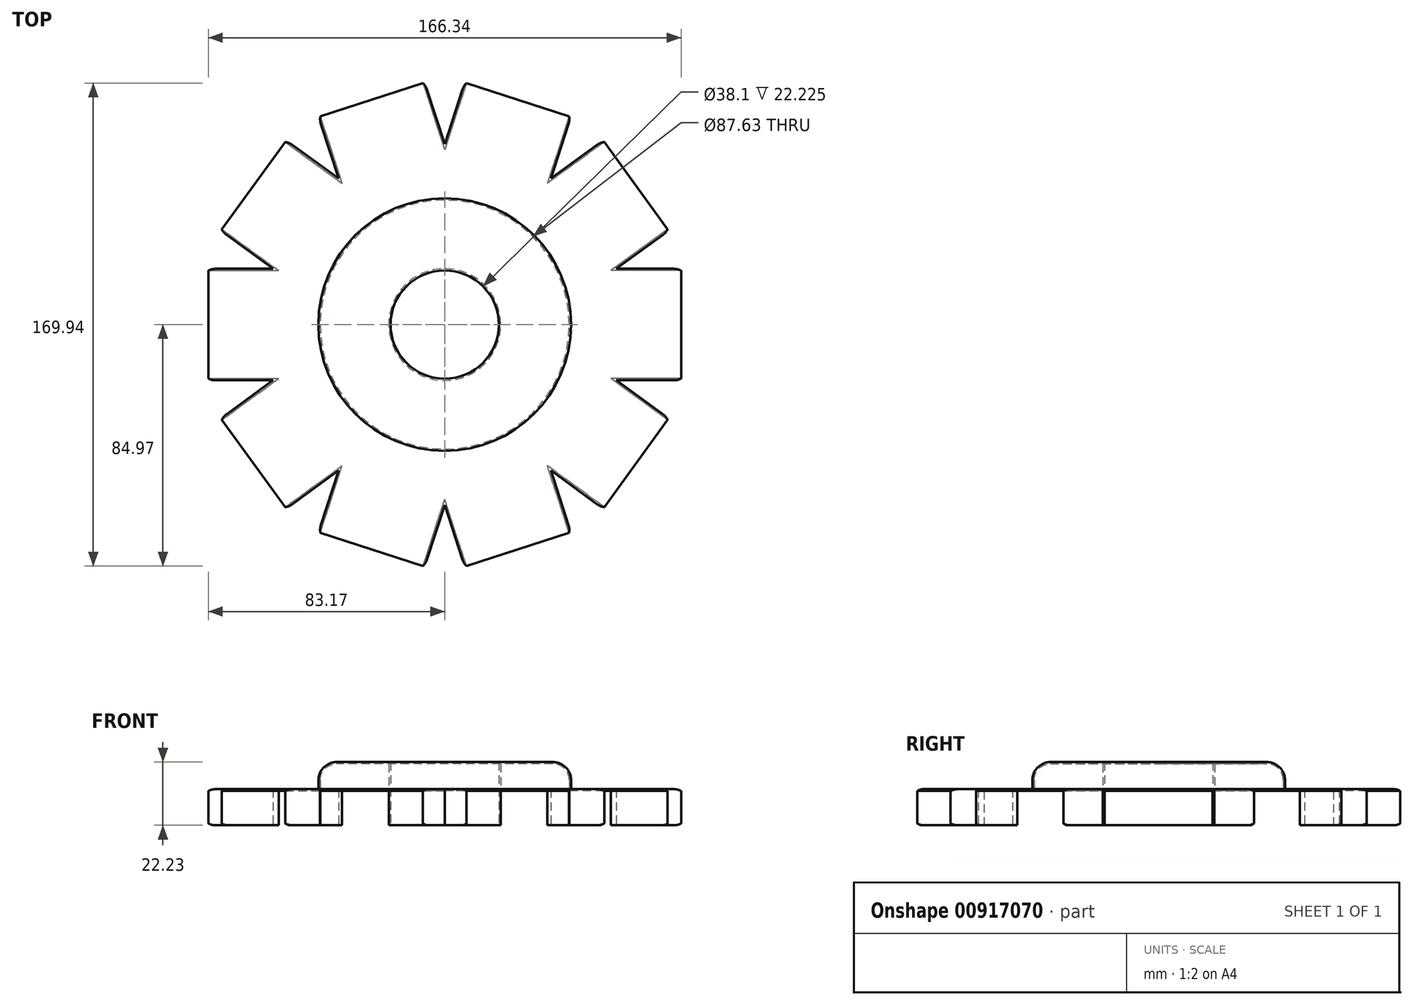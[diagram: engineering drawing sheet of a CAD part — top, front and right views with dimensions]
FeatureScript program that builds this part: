
annotation { "Feature Type Name" : "Feature", "Feature Type Description" : "" }
export const myFeature = defineFeature(function(context is Context, id is Id, definition is map)
    precondition{}
    {
        {
            var Q0;
            Q0=qCreatedBy(makeId("Top.planeOp"),FACE);
            var sketch = newSketch(context, id + "F0", { "sketchPlane" : qUnion([Q0])});
            skCircle(sketch, "E0.cCircle", {"center": v(0, 0) * mm, "radius": 63.5 * mm, "construction": true});
            skLineSegment(sketch, "E0.0", {"start": v(37.32, -51.37) * mm, "end": v(0, -63.5) * mm});
            skLineSegment(sketch, "E0.1", {"start": v(0, -63.5) * mm, "end": v(-37.32, -51.37) * mm});
            skLineSegment(sketch, "E0.2", {"start": v(-37.32, -51.37) * mm, "end": v(-60.4, -19.62) * mm});
            skLineSegment(sketch, "E0.3", {"start": v(-60.4, -19.62) * mm, "end": v(-60.4, 19.62) * mm});
            skLineSegment(sketch, "E0.4", {"start": v(-60.4, 19.62) * mm, "end": v(-37.32, 51.37) * mm});
            skLineSegment(sketch, "E0.5", {"start": v(-37.32, 51.37) * mm, "end": v(0, 63.5) * mm});
            skLineSegment(sketch, "E0.6", {"start": v(0, 63.5) * mm, "end": v(37.32, 51.37) * mm});
            skLineSegment(sketch, "E0.7", {"start": v(37.32, 51.37) * mm, "end": v(60.4, 19.62) * mm});
            skLineSegment(sketch, "E0.8", {"start": v(60.4, 19.62) * mm, "end": v(60.4, -19.62) * mm});
            skLineSegment(sketch, "E0.9", {"start": v(60.4, -19.62) * mm, "end": v(37.32, -51.37) * mm});
            skCircle(sketch, "E1", {"center": v(0, 0) * mm, "radius": 44.45 * mm});
            skCircle(sketch, "E2", {"center": v(0, 0) * mm, "radius": 12.7 * mm});
            skSolve(sketch);
        }
        {
            var Q0;
            Q0=makeQuery(id+"F0.imprint","IMPRINT",FACE,{"disambiguationData":[TD([[makeQuery(id+"F0.imprint","IMPRINT",EDGE,{"derivedFrom":sQuery(id+"F0.wireOp",EDGE,"E0.0")}),-1.0]])]});
            extrude(context, id + "F1", {"entities" : qUnion([Q0]), "depth" : 12.7 * mm, "offsetDistance" : 25.4 * mm});
        }
        {
            var Q0;
            Q0=makeQuery(id+"F1.opExtrude","SWEPT_FACE",FACE,{"disambiguationData":[OSD([sQuery(id+"F0.wireOp",EDGE,"E0.0")])]});
            extrude(context, id + "F2", {"entities" : qUnion([Q0]), "operationType" : NewBodyOperationType.ADD, "depth" : 25.4 * mm, "offsetDistance" : 25.4 * mm});
        }
        {
            var Q0;
            Q0=makeQuery(id+"F1.opExtrude","SWEPT_FACE",FACE,{"disambiguationData":[OSD([sQuery(id+"F0.wireOp",EDGE,"E0.5")])]});
            extrude(context, id + "F3", {"entities" : qUnion([Q0]), "operationType" : NewBodyOperationType.ADD, "depth" : 25.4 * mm, "offsetDistance" : 25.4 * mm});
        }
        {
            var Q0;
            Q0=makeQuery(id+"F1.opExtrude","SWEPT_FACE",FACE,{"disambiguationData":[OSD([sQuery(id+"F0.wireOp",EDGE,"E0.8")])]});
            extrude(context, id + "F4", {"entities" : qUnion([Q0]), "operationType" : NewBodyOperationType.ADD, "depth" : 25.4 * mm, "offsetDistance" : 25.4 * mm});
        }
        {
            var Q0;
            Q0=makeQuery(id+"F1.opExtrude","SWEPT_FACE",FACE,{"disambiguationData":[OSD([sQuery(id+"F0.wireOp",EDGE,"E0.7")])]});
            extrude(context, id + "F5", {"entities" : qUnion([Q0]), "operationType" : NewBodyOperationType.ADD, "depth" : 25.4 * mm, "offsetDistance" : 25.4 * mm});
        }
        {
            var Q0;
            Q0=makeQuery(id+"F1.opExtrude","SWEPT_FACE",FACE,{"disambiguationData":[OSD([sQuery(id+"F0.wireOp",EDGE,"E0.6")])]});
            extrude(context, id + "F6", {"entities" : qUnion([Q0]), "operationType" : NewBodyOperationType.ADD, "depth" : 25.4 * mm, "offsetDistance" : 25.4 * mm});
        }
        {
            var Q0;
            Q0=makeQuery(id+"F1.opExtrude","SWEPT_FACE",FACE,{"disambiguationData":[OSD([sQuery(id+"F0.wireOp",EDGE,"E0.9")])]});
            extrude(context, id + "F7", {"entities" : qUnion([Q0]), "operationType" : NewBodyOperationType.ADD, "depth" : 25.4 * mm, "offsetDistance" : 25.4 * mm});
        }
        {
            var Q0;
            Q0=makeQuery(id+"F1.opExtrude","SWEPT_FACE",FACE,{"disambiguationData":[OSD([sQuery(id+"F0.wireOp",EDGE,"E0.1")])]});
            extrude(context, id + "F8", {"entities" : qUnion([Q0]), "operationType" : NewBodyOperationType.ADD, "depth" : 25.4 * mm, "offsetDistance" : 25.4 * mm});
        }
        {
            var Q0;
            Q0=makeQuery(id+"F1.opExtrude","SWEPT_FACE",FACE,{"disambiguationData":[OSD([sQuery(id+"F0.wireOp",EDGE,"E0.2")])]});
            extrude(context, id + "F9", {"entities" : qUnion([Q0]), "operationType" : NewBodyOperationType.ADD, "depth" : 25.4 * mm, "offsetDistance" : 25.4 * mm});
        }
        {
            var Q0;
            Q0=makeQuery(id+"F1.opExtrude","SWEPT_FACE",FACE,{"disambiguationData":[OSD([sQuery(id+"F0.wireOp",EDGE,"E0.3")])]});
            extrude(context, id + "F10", {"entities" : qUnion([Q0]), "operationType" : NewBodyOperationType.ADD, "depth" : 25.4 * mm, "offsetDistance" : 25.4 * mm});
        }
        {
            var Q0;
            Q0=makeQuery(id+"F1.opExtrude","SWEPT_FACE",FACE,{"disambiguationData":[OSD([sQuery(id+"F0.wireOp",EDGE,"E0.4")])]});
            extrude(context, id + "F11", {"entities" : qUnion([Q0]), "operationType" : NewBodyOperationType.ADD, "depth" : 25.4 * mm, "offsetDistance" : 25.4 * mm});
        }
        {
            var Q0;
            Q0=qCreatedBy(makeId("Top.planeOp"),FACE);
            var sketch = newSketch(context, id + "F12", { "sketchPlane" : qUnion([Q0])});
            skCircle(sketch, "E3", {"center": v(0, 0) * mm, "radius": 19.05 * mm});
            skCircle(sketch, "E4", {"center": v(0, 0) * mm, "radius": 44.45 * mm});
            skSolve(sketch);
        }
        {
            var Q0;
            Q0=makeQuery(id+"F12.imprint","IMPRINT",FACE,{"disambiguationData":[TD([[makeQuery(id+"F12.imprint","IMPRINT",EDGE,{"derivedFrom":sQuery(id+"F12.wireOp",EDGE,"E3")}),-1.0]])]});
            extrude(context, id + "F13", {"entities" : qUnion([Q0]), "operationType" : NewBodyOperationType.ADD, "depth" : 22.22 * mm, "offsetDistance" : 25.4 * mm});
        }
        {
            var Q0;
            Q0=makeQuery(id+"F13.opExtrude","CAP_EDGE",EDGE,{"disambiguationData":[OSD([sQuery(id+"F12.wireOp",EDGE,"E4")])],"isStart":false});
            fillet(context, id + "F14", {"entities" : qUnion([Q0]), "radius" : 6.35 * mm, "tangentPropagation" : true, "allowEdgeOverflow" : false});
        }
        {
            var Q0;
            {var subQ0=sQuery(id+"F0.wireOp",EDGE,"E0.4");var subQ1=sQuery(id+"F0.wireOp",EDGE,"E0.3");var subQ2=sQuery(id+"F0.wireOp",EDGE,"E0.2");var subQ3=sQuery(id+"F0.wireOp",EDGE,"E0.1");var subQ4=sQuery(id+"F0.wireOp",EDGE,"E0.9");var subQ5=sQuery(id+"F0.wireOp",EDGE,"E0.6");var subQ6=sQuery(id+"F0.wireOp",EDGE,"E0.7");var subQ7=sQuery(id+"F0.wireOp",EDGE,"E0.8");var subQ8=sQuery(id+"F0.wireOp",EDGE,"E0.5");var subQ9=sQuery(id+"F0.wireOp",EDGE,"E0.0");Q0=makeQuery(id+"F13.boolean.opBoolean","MERGE",FACE,{"derivedFrom":[makeQuery(id+"F11.boolean.opBoolean","MERGE",FACE,{"derivedFrom":[makeQuery(id+"F10.boolean.opBoolean","MERGE",FACE,{"derivedFrom":[makeQuery(id+"F9.boolean.opBoolean","MERGE",FACE,{"derivedFrom":[makeQuery(id+"F8.boolean.opBoolean","MERGE",FACE,{"derivedFrom":[makeQuery(id+"F7.boolean.opBoolean","MERGE",FACE,{"derivedFrom":[makeQuery(id+"F6.boolean.opBoolean","MERGE",FACE,{"derivedFrom":[makeQuery(id+"F5.boolean.opBoolean","MERGE",FACE,{"derivedFrom":[makeQuery(id+"F4.boolean.opBoolean","MERGE",FACE,{"derivedFrom":[makeQuery(id+"F3.boolean.opBoolean","MERGE",FACE,{"derivedFrom":[makeQuery(id+"F2.boolean.opBoolean","MERGE",FACE,{"derivedFrom":[makeQuery(id+"F1.opExtrude","CAP_FACE",FACE,{"disambiguationData":[OSD([subQ9,subQ3,subQ2,subQ1,subQ0,subQ8,subQ5,subQ6,subQ7,subQ4,sQuery(id+"F0.wireOp",EDGE,"E1")])],"isStart":true}),makeQuery(id+"F2.opExtrude","SWEPT_FACE",FACE,{"disambiguationData":[OSD([subQ9]),TDD([makeQuery(id+"F1.opExtrude","CAP_EDGE",EDGE,{"disambiguationData":[OSD([subQ9])],"isStart":true})])]})]}),makeQuery(id+"F3.opExtrude","SWEPT_FACE",FACE,{"disambiguationData":[OSD([subQ8]),TDD([makeQuery(id+"F1.opExtrude","CAP_EDGE",EDGE,{"disambiguationData":[OSD([subQ8])],"isStart":true})])]})]}),makeQuery(id+"F4.opExtrude","SWEPT_FACE",FACE,{"disambiguationData":[OSD([subQ7]),TDD([makeQuery(id+"F1.opExtrude","CAP_EDGE",EDGE,{"disambiguationData":[OSD([subQ7])],"isStart":true})])]})]}),makeQuery(id+"F5.opExtrude","SWEPT_FACE",FACE,{"disambiguationData":[OSD([subQ6]),TDD([makeQuery(id+"F1.opExtrude","CAP_EDGE",EDGE,{"disambiguationData":[OSD([subQ6])],"isStart":true})])]})]}),makeQuery(id+"F6.opExtrude","SWEPT_FACE",FACE,{"disambiguationData":[OSD([subQ5]),TDD([makeQuery(id+"F1.opExtrude","CAP_EDGE",EDGE,{"disambiguationData":[OSD([subQ5])],"isStart":true})])]})]}),makeQuery(id+"F7.opExtrude","SWEPT_FACE",FACE,{"disambiguationData":[OSD([subQ4]),TDD([makeQuery(id+"F1.opExtrude","CAP_EDGE",EDGE,{"disambiguationData":[OSD([subQ4])],"isStart":true})])]})]}),makeQuery(id+"F8.opExtrude","SWEPT_FACE",FACE,{"disambiguationData":[OSD([subQ3]),TDD([makeQuery(id+"F1.opExtrude","CAP_EDGE",EDGE,{"disambiguationData":[OSD([subQ3])],"isStart":true})])]})]}),makeQuery(id+"F9.opExtrude","SWEPT_FACE",FACE,{"disambiguationData":[OSD([subQ2]),TDD([makeQuery(id+"F1.opExtrude","CAP_EDGE",EDGE,{"disambiguationData":[OSD([subQ2])],"isStart":true})])]})]}),makeQuery(id+"F10.opExtrude","SWEPT_FACE",FACE,{"disambiguationData":[OSD([subQ1]),TDD([makeQuery(id+"F1.opExtrude","CAP_EDGE",EDGE,{"disambiguationData":[OSD([subQ1])],"isStart":true})])]})]}),makeQuery(id+"F11.opExtrude","SWEPT_FACE",FACE,{"disambiguationData":[OSD([subQ0]),TDD([makeQuery(id+"F1.opExtrude","CAP_EDGE",EDGE,{"disambiguationData":[OSD([subQ0])],"isStart":true})])]})]}),makeQuery(id+"F13.opExtrude","CAP_FACE",FACE,{"disambiguationData":[OSD([sQuery(id+"F12.wireOp",EDGE,"E3"),sQuery(id+"F12.wireOp",EDGE,"E4")])],"isStart":true})]});}
            shell(context, id + "F15", {"entities" : qUnion([Q0]), "thickness" : 0.64 * mm});
        }
        {
            var Q0;
            Q0=makeQuery(id+"F2.opExtrude","CAP_FACE",FACE,{"disambiguationData":[OSD([sQuery(id+"F0.wireOp",EDGE,"E0.0")])],"isStart":false});
            fillet(context, id + "F16", {"entities" : qUnion([Q0]), "radius" : 5.08 * mm, "tangentPropagation" : true, "allowEdgeOverflow" : false});
        }
        {
            var Q0;
            Q0=makeQuery(id+"F7.opExtrude","CAP_FACE",FACE,{"disambiguationData":[OSD([sQuery(id+"F0.wireOp",EDGE,"E0.9")])],"isStart":false});
            fillet(context, id + "F17", {"entities" : qUnion([Q0]), "radius" : 5.08 * mm, "tangentPropagation" : true, "allowEdgeOverflow" : false});
        }
        {
            var Q0;
            Q0=makeQuery(id+"F4.opExtrude","CAP_FACE",FACE,{"disambiguationData":[OSD([sQuery(id+"F0.wireOp",EDGE,"E0.8")])],"isStart":false});
            var Q1;
            Q1=makeQuery(id+"F5.opExtrude","CAP_FACE",FACE,{"disambiguationData":[OSD([sQuery(id+"F0.wireOp",EDGE,"E0.7")])],"isStart":false});
            var Q2;
            Q2=makeQuery(id+"F6.opExtrude","CAP_FACE",FACE,{"disambiguationData":[OSD([sQuery(id+"F0.wireOp",EDGE,"E0.6")])],"isStart":false});
            var Q3;
            Q3=makeQuery(id+"F3.opExtrude","CAP_FACE",FACE,{"disambiguationData":[OSD([sQuery(id+"F0.wireOp",EDGE,"E0.5")])],"isStart":false});
            var Q4;
            Q4=makeQuery(id+"F11.opExtrude","CAP_FACE",FACE,{"disambiguationData":[OSD([sQuery(id+"F0.wireOp",EDGE,"E0.4")])],"isStart":false});
            var Q5;
            Q5=makeQuery(id+"F10.opExtrude","CAP_FACE",FACE,{"disambiguationData":[OSD([sQuery(id+"F0.wireOp",EDGE,"E0.3")])],"isStart":false});
            var Q6;
            Q6=makeQuery(id+"F9.opExtrude","CAP_FACE",FACE,{"disambiguationData":[OSD([sQuery(id+"F0.wireOp",EDGE,"E0.2")])],"isStart":false});
            var Q7;
            Q7=makeQuery(id+"F8.opExtrude","CAP_FACE",FACE,{"disambiguationData":[OSD([sQuery(id+"F0.wireOp",EDGE,"E0.1")])],"isStart":false});
            fillet(context, id + "F18", {"entities" : qUnion([Q0, Q1, Q2, Q3, Q4, Q5, Q6, Q7]), "radius" : 5.08 * mm, "tangentPropagation" : true, "allowEdgeOverflow" : false});
        }
    });
